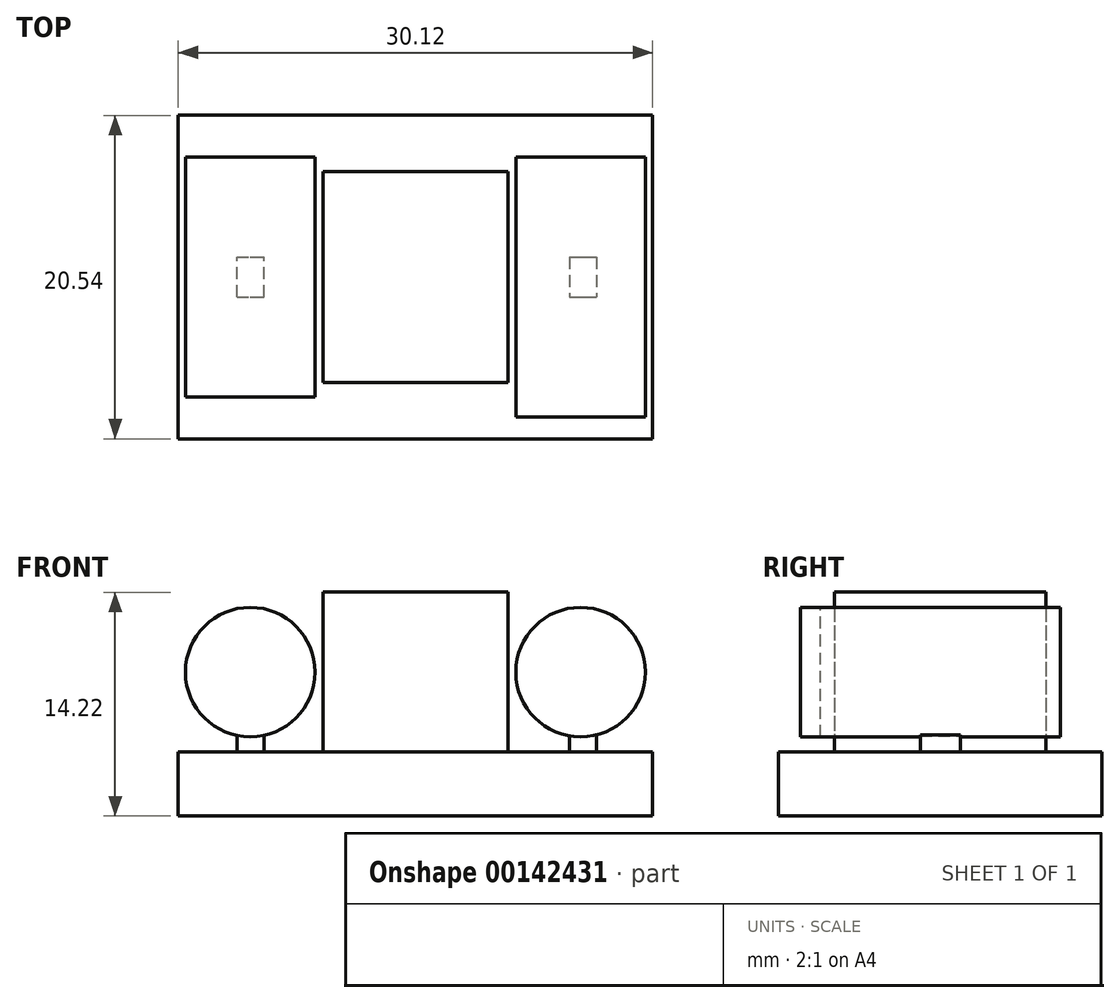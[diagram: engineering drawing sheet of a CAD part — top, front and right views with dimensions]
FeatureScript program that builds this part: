
annotation { "Feature Type Name" : "Feature", "Feature Type Description" : "" }
export const myFeature = defineFeature(function(context is Context, id is Id, definition is map)
    precondition{}
    {
        {
            var Q0;
            Q0=qCreatedBy(makeId("Top.planeOp"),FACE);
            var sketch = newSketch(context, id + "F0", { "sketchPlane" : qUnion([Q0])});
            skLineSegment(sketch, "E0.bottom", {"start": v(15.06, -10.27) * mm, "end": v(-15.06, -10.27) * mm});
            skLineSegment(sketch, "E0.top", {"start": v(15.06, 10.27) * mm, "end": v(-15.06, 10.27) * mm});
            skLineSegment(sketch, "E0.left", {"start": v(15.06, -10.27) * mm, "end": v(15.06, 10.27) * mm});
            skLineSegment(sketch, "E0.right", {"start": v(-15.06, -10.27) * mm, "end": v(-15.06, 10.27) * mm});
            skPoint(sketch, "E0.middle", {"position": v(0, 0) * mm});
            skSolve(sketch);
        }
        {
            var Q0;
            Q0 = qSketchRegion(id + "F0", true);
            extrude(context, id + "F1", {"entities" : qUnion([Q0]), "depth" : 4.06 * mm});
        }
        {
            var Q0;
            Q0=makeQuery(id+"F1.opExtrude","CAP_FACE",FACE,{"disambiguationData":[OSD([sQuery(id+"F0.wireOp",EDGE,"E0.bottom"),sQuery(id+"F0.wireOp",EDGE,"E0.top"),sQuery(id+"F0.wireOp",EDGE,"E0.left"),sQuery(id+"F0.wireOp",EDGE,"E0.right")])],"isStart":false});
            var sketch = newSketch(context, id + "F2", { "sketchPlane" : qUnion([Q0])});
            skLineSegment(sketch, "E1.bottom", {"start": v(5.87, -6.7) * mm, "end": v(-5.87, -6.7) * mm});
            skLineSegment(sketch, "E1.top", {"start": v(5.87, 6.7) * mm, "end": v(-5.87, 6.7) * mm});
            skLineSegment(sketch, "E1.left", {"start": v(5.87, -6.7) * mm, "end": v(5.87, 6.7) * mm});
            skLineSegment(sketch, "E1.right", {"start": v(-5.87, -6.7) * mm, "end": v(-5.87, 6.7) * mm});
            skPoint(sketch, "E1.middle", {"position": v(0, 0) * mm});
            skSolve(sketch);
        }
        {
            var Q0;
            Q0 = qSketchRegion(id + "F2", true);
            extrude(context, id + "F3", {"entities" : qUnion([Q0]), "operationType" : NewBodyOperationType.ADD, "depth" : 10.16 * mm});
        }
        {
            var Q0;
            Q0=qCreatedBy(makeId("Front.planeOp"),FACE);
            var sketch = newSketch(context, id + "F4", { "sketchPlane" : qUnion([Q0])});
            skCircle(sketch, "E2", {"center": v(10.5, 9.14) * mm, "radius": 4.11 * mm});
            skCircle(sketch, "E3", {"center": v(-10.5, 9.14) * mm, "radius": 4.11 * mm});
            skSolve(sketch);
        }
        {
            var Q0;
            Q0 = qSketchRegion(id + "F4", true);
            extrude(context, id + "F5", {"entities" : qUnion([Q0]), "operationType" : NewBodyOperationType.ADD, "endBound" : BoundingType.SYMMETRIC, "depth" : 15.24 * mm});
        }
        {
            var Q0;
            Q0=qCreatedBy(makeId("Front.planeOp"),FACE);
            var sketch = newSketch(context, id + "F6", { "sketchPlane" : qUnion([Q0])});
            skLineSegment(sketch, "E4.bottom", {"start": v(-9.63, 8.48) * mm, "end": v(-11.34, 8.48) * mm});
            skLineSegment(sketch, "E4.top", {"start": v(-9.63, 1.58) * mm, "end": v(-11.34, 1.58) * mm});
            skLineSegment(sketch, "E4.left", {"start": v(-9.63, 8.48) * mm, "end": v(-9.63, 1.58) * mm});
            skLineSegment(sketch, "E4.right", {"start": v(-11.34, 8.48) * mm, "end": v(-11.34, 1.58) * mm});
            skPoint(sketch, "E4.middle", {"position": v(-10.49, 5.03) * mm});
            skLineSegment(sketch, "E5.bottom", {"start": v(11.52, 1.59) * mm, "end": v(9.8, 1.59) * mm});
            skLineSegment(sketch, "E5.top", {"start": v(11.52, 8.48) * mm, "end": v(9.8, 8.48) * mm});
            skLineSegment(sketch, "E5.left", {"start": v(11.52, 1.59) * mm, "end": v(11.52, 8.48) * mm});
            skLineSegment(sketch, "E5.right", {"start": v(9.8, 1.59) * mm, "end": v(9.8, 8.48) * mm});
            skPoint(sketch, "E5.middle", {"position": v(10.66, 5.03) * mm});
            skSolve(sketch);
        }
        {
            var Q0;
            Q0=makeQuery(id+"F6.imprint","IMPRINT",FACE,{"disambiguationData":[TD([[makeQuery(id+"F6.imprint","IMPRINT",EDGE,{"derivedFrom":sQuery(id+"F6.wireOp",EDGE,"E4.bottom")}),1.0]])]});
            var Q1;
            Q1=makeQuery(id+"F5.opExtrude","CAP_FACE",FACE,{"disambiguationData":[OSD([sQuery(id+"F4.wireOp",EDGE,"E2")])],"isStart":false});
            var Q2;
            Q2=makeQuery(id+"F6.imprint","IMPRINT",FACE,{"disambiguationData":[TD([[makeQuery(id+"F6.imprint","IMPRINT",EDGE,{"derivedFrom":sQuery(id+"F6.wireOp",EDGE,"E5.bottom")}),-1.0]])]});
            extrude(context, id + "F7", {"entities" : qUnion([Q0, Q1, Q2]), "operationType" : NewBodyOperationType.ADD, "endBound" : BoundingType.SYMMETRIC, "depth" : 2.54 * mm});
        }
    });
